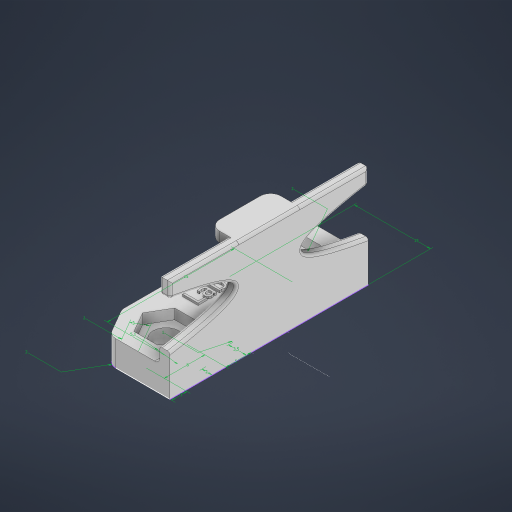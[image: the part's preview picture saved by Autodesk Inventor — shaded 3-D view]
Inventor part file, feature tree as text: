
AUTODESK INVENTOR PART (.ipt)
format: ipt  version: 2024.1 (Build 281209000, 209)  size: 605,184 bytes
history: native  units: in
note: dims shown in document units (in); Inventor stores cm internally (conversion verified against a paired STEP export)
features: extrude x7, sketch x4, fillet x4
ambient origin geometry x8: Origin, YZ Plane, XZ Plane, XY Plane, X Axis, Y Axis, Z Axis, Center Point
bodies: Body1 (feature_tree)
feature tree (15):
  sketch  "Sketch2"  dims[d18=0.315in d19=0.2008in]
  extrude  "Extrusion9"  Depth=0.2008in
  extrude  "Extrusion10"  Depth=0.1181in
  extrude  "Extrusion13"  Depth=0.0787in
  extrude  "Extrusion14"  Depth=0.0157in
  extrude  "Extrusion15"  Depth=0.0157in
  fillet  "Fillet3"  Radius=0.0394in
  fillet  "Fillet4"  Radius=0.1378in
  fillet  "Fillet5"  Radius=0.5906in
  extrude  "Extrusion16"  Depth=0.0157in
  fillet  "Fillet6"  Radius=0.1969in
  extrude  "Extrusion17"  Depth=0.0157in TaperAngle=0.0deg
  sketch  "Sketch6"  dims[d21=0.1181in d22=0.1181in]
  sketch  "Sketch7"  dims[d27=0.9843in d35=0.0787in]
  sketch  "Sketch8"  dims[d36=0.0787in d37=0.0787in d49=0.1969in d50=0.0394in d51=0.1378in d52=0.5906in d53=0.0787in d54=0.1969in d55=0.0in d56=0.1181in d57=0.0in d69=0.7874in d70=0.0in d71=0.7087in d72=0.0in d73=0.1181in d74=0.1181in d75=0.1181in d76=0.7874in d77=0.0in d78=0.0394in d79=0.0197in d80=0.0201in d82=0.2362in d83=0.4724in d84=0.0787in d85=0.0787in d86=0.0in d87=0.0197in d90=0.0157in d91=0.0in d92=0.0816in d93=0.0952in d45=0.0197in d46=0.0344in d47=0.0197in d48=0.0344in d67=0.0in d68=0.0in]
